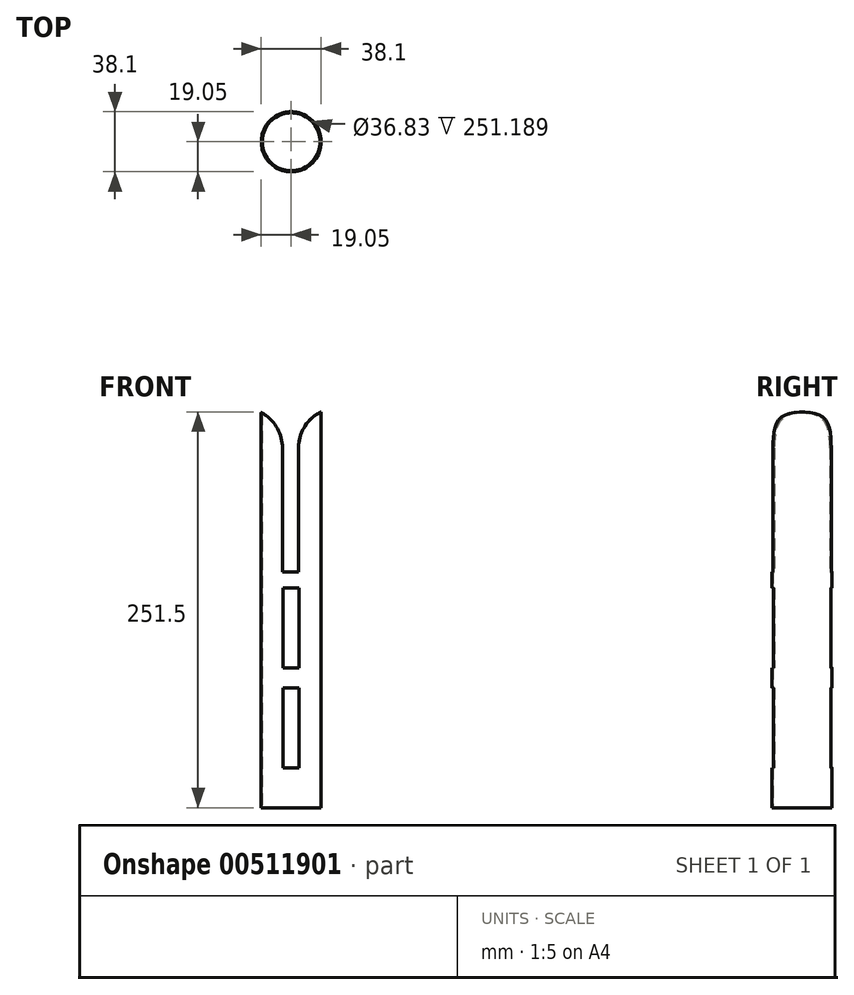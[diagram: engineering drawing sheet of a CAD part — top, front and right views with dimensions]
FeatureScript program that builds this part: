
annotation { "Feature Type Name" : "Feature", "Feature Type Description" : "" }
export const myFeature = defineFeature(function(context is Context, id is Id, definition is map)
    precondition{}
    {
        {
            var Q0;
            Q0=qCreatedBy(makeId("Top.planeOp"),FACE);
            var sketch = newSketch(context, id + "F0", { "sketchPlane" : qUnion([Q0])});
            skCircle(sketch, "E0", {"center": v(0, 0) * mm, "radius": 19.05 * mm});
            skSolve(sketch);
        }
        {
            var Q0;
            Q0=makeQuery(id+"F0.imprint","IMPRINT",FACE,{"disambiguationData":[TD([[makeQuery(id+"F0.imprint","IMPRINT",EDGE,{"derivedFrom":sQuery(id+"F0.wireOp",EDGE,"E0")}),1.0]])]});
            extrude(context, id + "F1", {"entities" : qUnion([Q0]), "depth" : 254 * mm, "offsetDistance" : 25.4 * mm});
        }
        {
            var Q0;
            Q0=makeQuery(id+"F1.opExtrude","CAP_FACE",FACE,{"disambiguationData":[OSD([sQuery(id+"F0.wireOp",EDGE,"E0")])],"isStart":true});
            var Q1;
            Q1=makeQuery(id+"F1.opExtrude","CAP_FACE",FACE,{"disambiguationData":[OSD([sQuery(id+"F0.wireOp",EDGE,"E0")])],"isStart":false});
            shell(context, id + "F2", {"entities" : qUnion([Q0, Q1]), "thickness" : 0.64 * mm});
        }
        {
            var Q0;
            Q0=qCreatedBy(makeId("Front.planeOp"),FACE);
            var sketch = newSketch(context, id + "F3", { "sketchPlane" : qUnion([Q0])});
            skLineSegment(sketch, "E1.bottom", {"start": v(5.08, 76.2) * mm, "end": v(-5.08, 76.2) * mm});
            skLineSegment(sketch, "E1.top", {"start": v(5.08, 25.4) * mm, "end": v(-5.08, 25.4) * mm});
            skLineSegment(sketch, "E1.left", {"start": v(5.08, 76.2) * mm, "end": v(5.08, 25.4) * mm});
            skLineSegment(sketch, "E1.right", {"start": v(-5.08, 76.2) * mm, "end": v(-5.08, 25.4) * mm});
            skPoint(sketch, "E1.middle", {"position": v(0, 50.8) * mm});
            skLineSegment(sketch, "E2.bottom", {"start": v(5.08, 139.7) * mm, "end": v(-5.08, 139.7) * mm});
            skLineSegment(sketch, "E2.top", {"start": v(5.08, 88.9) * mm, "end": v(-5.08, 88.9) * mm});
            skLineSegment(sketch, "E2.left", {"start": v(5.08, 139.7) * mm, "end": v(5.08, 88.9) * mm});
            skLineSegment(sketch, "E2.right", {"start": v(-5.08, 139.7) * mm, "end": v(-5.08, 88.9) * mm});
            skPoint(sketch, "E2.middle", {"position": v(0, 114.3) * mm});
            skLineSegment(sketch, "E3.bottom", {"start": v(4.64, 276.86) * mm, "end": v(-5.52, 276.86) * mm});
            skLineSegment(sketch, "E3.top", {"start": v(4.64, 149.86) * mm, "end": v(-5.52, 149.86) * mm});
            skLineSegment(sketch, "E3.left", {"start": v(4.64, 276.86) * mm, "end": v(4.64, 149.86) * mm});
            skLineSegment(sketch, "E3.right", {"start": v(-5.52, 276.86) * mm, "end": v(-5.52, 149.86) * mm});
            skPoint(sketch, "E3.middle", {"position": v(-0.44, 213.36) * mm});
            skSolve(sketch);
        }
        {
            var Q0;
            Q0 = qSketchRegion(id + "F3", true);
            extrude(context, id + "F4", {"entities" : qUnion([Q0]), "operationType" : NewBodyOperationType.REMOVE, "endBound" : BoundingType.SYMMETRIC, "depth" : 76.2 * mm});
        }
        {
            var Q0;
            Q0=makeQuery(id+"F4.boolean.opBoolean","INTERSECT",EDGE,{"disambiguationData":[OD(0.0)],"derivedFrom":[makeQuery(id+"F1.opExtrude","CAP_FACE",FACE,{"disambiguationData":[OSD([sQuery(id+"F0.wireOp",EDGE,"E0")])],"isStart":false}),makeQuery(id+"F4.opExtrude","SWEPT_FACE",FACE,{"disambiguationData":[OSD([sQuery(id+"F3.wireOp",EDGE,"E3.left")])]})]});
            var Q1;
            Q1=makeQuery(id+"F4.boolean.opBoolean","INTERSECT",EDGE,{"disambiguationData":[OD(1.0)],"derivedFrom":[makeQuery(id+"F1.opExtrude","CAP_FACE",FACE,{"disambiguationData":[OSD([sQuery(id+"F0.wireOp",EDGE,"E0")])],"isStart":false}),makeQuery(id+"F4.opExtrude","SWEPT_FACE",FACE,{"disambiguationData":[OSD([sQuery(id+"F3.wireOp",EDGE,"E3.right")])]})]});
            fillet(context, id + "F5", {"entities" : qUnion([Q0, Q1]), "radius" : 25.4 * mm, "allowEdgeOverflow" : false});
        }
    });
